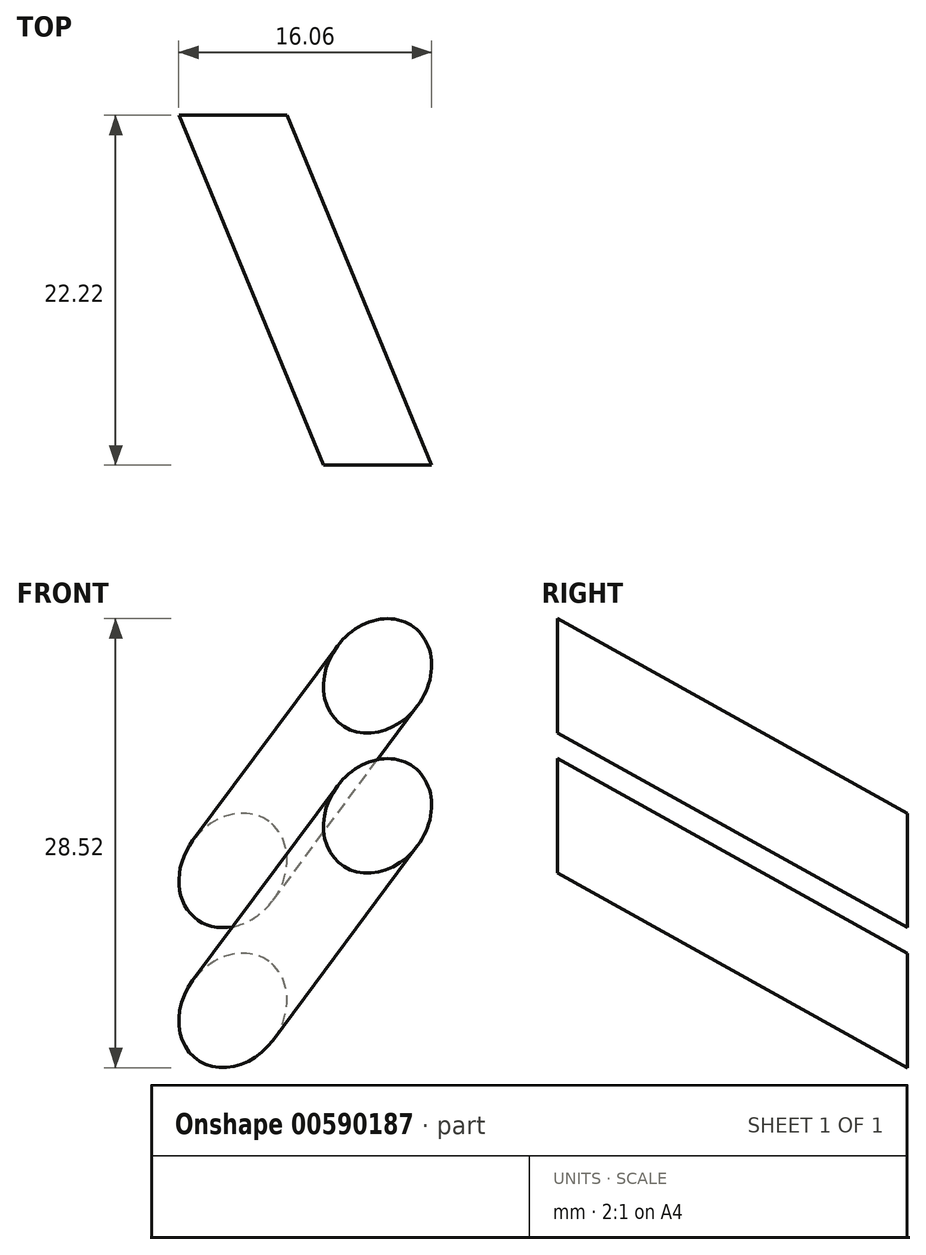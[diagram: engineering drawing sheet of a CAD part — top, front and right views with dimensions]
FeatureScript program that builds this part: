
annotation { "Feature Type Name" : "Feature", "Feature Type Description" : "" }
export const myFeature = defineFeature(function(context is Context, id is Id, definition is map)
    precondition{}
    {
        {
            assignVariable(context, id + "F0", {"name" : "alpha", "anyValue" : 27.2 * degree});
        }
        {
            var Q0;
            Q0=qCreatedBy(makeId("Front.planeOp"),FACE);
            var sketch = newSketch(context, id + "F1", { "sketchPlane" : qUnion([Q0])});
            skCircle(sketch, "E0", {"center": v(0, 0) * mm, "radius": 17.08 * mm});
            skSolve(sketch);
        }
        {
            var Q0;
            Q0 = qSketchRegion(id + "F1", true);
            var Q1;
            Q1=sQuery(id+"F1.wireOp",EDGE,"E0");
            extrude(context, id + "F2", {"entities" : qUnion([Q0]), "bodyType" : ToolBodyType.SURFACE, "surfaceEntities" : qUnion([Q1]), "depth" : 11.1 * mm, "offsetDistance" : 25.4 * mm, "hasSecondDirection" : true, "secondDirectionOppositeDirection" : true, "secondDirectionDepth" : 11.1 * mm});
        }
        {
            var Q0;
            Q0=qCreatedBy(makeId("Top.planeOp"),FACE);
            var sketch = newSketch(context, id + "F3", { "sketchPlane" : qUnion([Q0])});
            skLineSegment(sketch, "E1", {"start": v(13.48, -11.11) * mm, "end": v(4.3, 11.11) * mm, "construction": true});
            skPoint(sketch, "E2", {"position": v(8.9, 0) * mm});
            skLineSegment(sketch, "E3", {"start": v(8.89, 0) * mm, "end": v(20.57, 4.82) * mm, "construction": true});
            skSolve(sketch);
        }
        {
            var Q0;
            Q0=sQuery(id+"F3.wireOp",EDGE,"E1");
            cPlane(context, id + "F4", {"entities" : qUnion([Q0]), "cplaneType" : CPlaneType.LINE_ANGLE, "offset" : 25.4 * mm, "angle" : 90 * degree, "width" : 152.4 * mm, "height" : 152.4 * mm});
        }
        {
            var Q0;
            Q0=sQuery(id+"F3.wireOp",EDGE,"E3");
            var Q1;
            Q1=qCreatedBy(makeId("Right.planeOp"),FACE);
            cPlane(context, id + "F5", {"entities" : qUnion([Q0, Q1]), "cplaneType" : CPlaneType.LINE_ANGLE, "offset" : 25.4 * mm, "angle" : getVariable(context, 'alpha'), "oppositeDirection" : true, "width" : 152.4 * mm, "height" : 152.4 * mm});
        }
        {
            var Q0;
            Q0=qCreatedBy(id+"F5.planeOp",FACE);
            var sketch = newSketch(context, id + "F6", { "sketchPlane" : qUnion([Q0])});
            skCircle(sketch, "E4", {"center": v(-6.74, 8.6) * mm, "radius": 3.17 * mm});
            skSolve(sketch);
        }
        {
            var Q0;
            Q0=qCreatedBy(id+"F5.planeOp",FACE);
            var sketch = newSketch(context, id + "F7", { "sketchPlane" : qUnion([Q0])});
            skCircle(sketch, "E5", {"center": v(-5.27, 16.38) * mm, "radius": 3.17 * mm});
            skSolve(sketch);
        }
        {
            var Q0;
            Q0=qCreatedBy(makeId("Front.planeOp"),FACE);
            cPlane(context, id + "F8", {"entities" : qUnion([Q0]), "cplaneType" : CPlaneType.OFFSET, "offset" : 11.1 * mm, "oppositeDirection" : true, "width" : 152.4 * mm, "height" : 152.4 * mm});
        }
        {
            var Q0;
            Q0=qCreatedBy(makeId("Front.planeOp"),FACE);
            cPlane(context, id + "F9", {"entities" : qUnion([Q0]), "cplaneType" : CPlaneType.OFFSET, "offset" : 11.1 * mm, "width" : 152.4 * mm, "height" : 152.4 * mm});
        }
        {
            var Q0;
            Q0 = qSketchRegion(id + "F6", true);
            var Q1;
            Q1=qCreatedBy(id+"F8.planeOp",FACE);
            var Q2;
            Q2=qCreatedBy(id+"F9.planeOp",FACE);
            extrude(context, id + "F10", {"entities" : qUnion([Q0]), "endBound" : BoundingType.UP_TO_SURFACE, "depth" : 25.4 * mm, "endBoundEntityFace" : qUnion([Q1]), "offsetDistance" : 25.4 * mm, "hasSecondDirection" : true, "secondDirectionBound" : SecondDirectionBoundingType.UP_TO_SURFACE, "secondDirectionOppositeDirection" : true, "secondDirectionDepth" : 25.4 * mm, "secondDirectionBoundEntityFace" : qUnion([Q2])});
        }
        {
            var Q0;
            Q0=makeQuery(id+"F7.imprint","IMPRINT",FACE,{"disambiguationData":[TD([[makeQuery(id+"F7.imprint","IMPRINT",EDGE,{"derivedFrom":sQuery(id+"F7.wireOp",EDGE,"E5")}),1.0]])]});
            var Q1;
            Q1=sQuery(id+"F7.wireOp",EDGE,"E5");
            var Q2;
            Q2=qCreatedBy(id+"F8.planeOp",FACE);
            var Q3;
            Q3=qCreatedBy(id+"F9.planeOp",FACE);
            extrude(context, id + "F11", {"entities" : qUnion([Q0]), "surfaceEntities" : qUnion([Q1]), "endBound" : BoundingType.UP_TO_SURFACE, "depth" : 25.4 * mm, "endBoundEntityFace" : qUnion([Q2]), "offsetDistance" : 25.4 * mm, "hasSecondDirection" : true, "secondDirectionBound" : SecondDirectionBoundingType.UP_TO_SURFACE, "secondDirectionOppositeDirection" : true, "secondDirectionDepth" : 25.4 * mm, "secondDirectionBoundEntityFace" : qUnion([Q3])});
        }
        {
            var Q0;
            Q0=qCreatedBy(id+"F8.planeOp",FACE);
            var sketch = newSketch(context, id + "F12", { "sketchPlane" : qUnion([Q0])});
            skPoint(sketch, "E6", {"position": v(5.95, 16.01) * mm});
            skSolve(sketch);
        }
        {
            var Q0;
            Q0=qCreatedBy(id+"F9.planeOp",FACE);
            var sketch = newSketch(context, id + "F13", { "sketchPlane" : qUnion([Q0])});
            skPoint(sketch, "E7", {"position": v(11.05, 13.03) * mm});
            skSolve(sketch);
        }
        {
            var Q0;
            Q0=qCreatedBy(id+"F5.planeOp",FACE);
            var Q1;
            Q1=sQuery(id+"F13.wireOp",VERTEX,"E7");
            cPlane(context, id + "F14", {"entities" : qUnion([Q0, Q1]), "cplaneType" : CPlaneType.PLANE_POINT, "offset" : 25.4 * mm, "width" : 152.4 * mm, "height" : 152.4 * mm});
        }
        {
            var Q0;
            Q0=qCreatedBy(id+"F5.planeOp",FACE);
            var Q1;
            Q1=sQuery(id+"F12.wireOp",VERTEX,"E6");
            cPlane(context, id + "F15", {"entities" : qUnion([Q0, Q1]), "cplaneType" : CPlaneType.PLANE_POINT, "offset" : 25.4 * mm, "width" : 152.4 * mm, "height" : 152.4 * mm});
        }
        {
            var Q0;
            Q0=qCreatedBy(id+"F14.planeOp",FACE);
            var sketch = newSketch(context, id + "F16", { "sketchPlane" : qUnion([Q0])});
            skCircle(sketch, "E8", {"center": v(-6.74, 8.6) * mm, "radius": 3.17 * mm});
            skSolve(sketch);
        }
        {
            var Q0;
            Q0=qCreatedBy(id+"F4.planeOp",FACE);
            var sketch = newSketch(context, id + "F17", { "sketchPlane" : qUnion([Q0])});
            skLineSegment(sketch, "E9", {"start": v(-13.46, 15.02) * mm, "end": v(-15.42, 16.03) * mm, "construction": true});
            skSolve(sketch);
        }
        {
            var Q0;
            Q0=qCreatedBy(id+"F9.planeOp",FACE);
            var sketch = newSketch(context, id + "F18", { "sketchPlane" : qUnion([Q0])});
            skLineSegment(sketch, "E10", {"start": v(13.48, 0) * mm, "end": v(13.48, 10.5) * mm, "construction": true});
            skLineSegment(sketch, "E11", {"start": v(13.48, 10.5) * mm, "end": v(13.48, 16.03) * mm, "construction": true});
            skLineSegment(sketch, "E12", {"start": v(13.48, 16.03) * mm, "end": v(11.05, 13.03) * mm, "construction": true});
            skLineSegment(sketch, "E13", {"start": v(1.85, 1.72) * mm, "end": v(11.05, 13.03) * mm, "construction": true});
            skSolve(sketch);
        }
        {
            var Q0;
            Q0=qCreatedBy(id+"F8.planeOp",FACE);
            var sketch = newSketch(context, id + "F19", { "sketchPlane" : qUnion([Q0])});
            skLineSegment(sketch, "E14", {"start": v(4.3, 16.53) * mm, "end": v(4.3, 0) * mm, "construction": true});
            skSolve(sketch);
        }
        {
            var Q0;
            Q0=qCreatedBy(id+"F14.planeOp",FACE);
            var sketch = newSketch(context, id + "F20", { "sketchPlane" : qUnion([Q0])});
            skPoint(sketch, "E15", {"position": v(-7.33, 5.48) * mm});
            skSolve(sketch);
        }
        {
            var Q0;
            Q0=qCreatedBy(id+"F4.planeOp",FACE);
            var sketch = newSketch(context, id + "F21", { "sketchPlane" : qUnion([Q0])});
            skLineSegment(sketch, "E16", {"start": v(-15.42, 10.5) * mm, "end": v(-15.42, 15.6) * mm, "construction": true});
            skLineSegment(sketch, "E17", {"start": v(-12.01, 17.85) * mm, "end": v(-14.92, 12.2) * mm, "construction": true});
            skSolve(sketch);
        }
        {
            var Q0;
            Q0=qCreatedBy(id+"F14.planeOp",FACE);
            var sketch = newSketch(context, id + "F22", { "sketchPlane" : qUnion([Q0])});
            skLineSegment(sketch, "E18", {"start": v(-6.74, 8.6) * mm, "end": v(-4.94, 5.99) * mm, "construction": true});
            skLineSegment(sketch, "E19", {"start": v(-4.94, 5.99) * mm, "end": v(4.53, -7.82) * mm, "construction": true});
            skSolve(sketch);
        }
        {
            var Q0;
            Q0=qCreatedBy(id+"F8.planeOp",FACE);
            var sketch = newSketch(context, id + "F23", { "sketchPlane" : qUnion([Q0])});
            skPoint(sketch, "E20", {"position": v(0, 0) * mm});
            skSolve(sketch);
        }
        {
            var Q0;
            Q0=qCreatedBy(id+"F4.planeOp",FACE);
            var Q1;
            Q1=sQuery(id+"F18.wireOp",VERTEX,"E13.start");
            cPlane(context, id + "F24", {"entities" : qUnion([Q0, Q1]), "cplaneType" : CPlaneType.PLANE_POINT, "offset" : 25.4 * mm, "width" : 152.4 * mm, "height" : 152.4 * mm});
        }
    });
